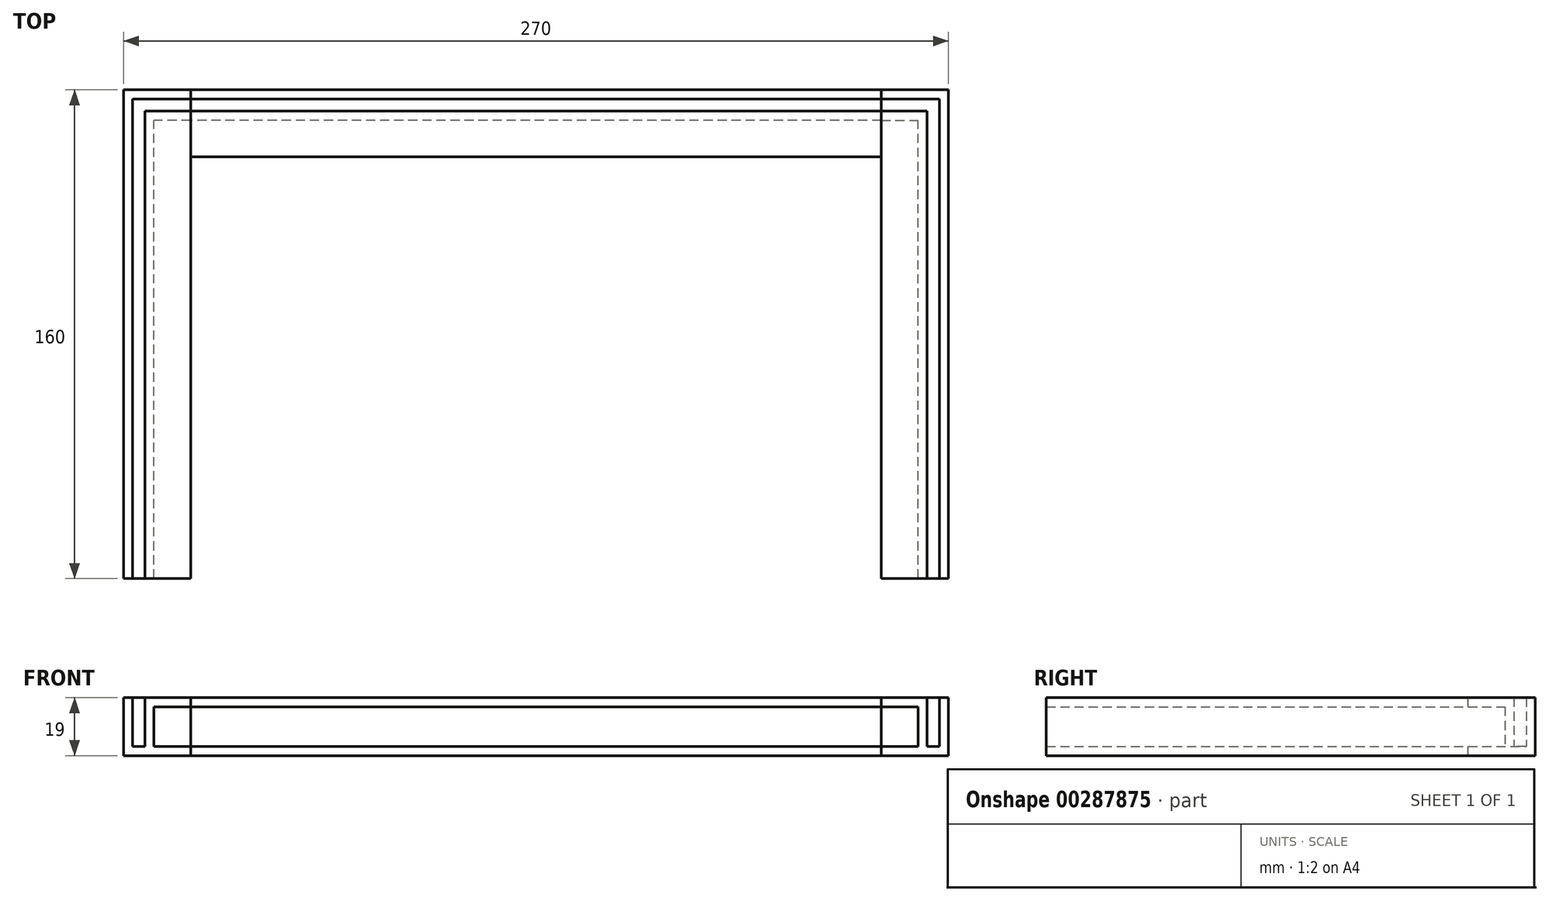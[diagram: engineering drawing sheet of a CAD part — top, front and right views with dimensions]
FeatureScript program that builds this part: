
annotation { "Feature Type Name" : "Feature", "Feature Type Description" : "" }
export const myFeature = defineFeature(function(context is Context, id is Id, definition is map)
    precondition{}
    {
        {
            var Q0;
            Q0=qCreatedBy(makeId("Front.planeOp"),FACE);
            var sketch = newSketch(context, id + "F0", { "sketchPlane" : qUnion([Q0])});
            skLineSegment(sketch, "E0", {"start": v(0, 0) * mm, "end": v(0, 19) * mm});
            skLineSegment(sketch, "E1", {"start": v(0, 19) * mm, "end": v(3, 19) * mm});
            skLineSegment(sketch, "E2", {"start": v(3, 19) * mm, "end": v(3, 3) * mm});
            skLineSegment(sketch, "E3", {"start": v(3, 3) * mm, "end": v(7, 3) * mm});
            skLineSegment(sketch, "E4", {"start": v(7, 3) * mm, "end": v(7, 19) * mm});
            skLineSegment(sketch, "E5", {"start": v(7, 19) * mm, "end": v(22, 19) * mm});
            skLineSegment(sketch, "E6", {"start": v(22, 19) * mm, "end": v(22, 16) * mm});
            skLineSegment(sketch, "E7", {"start": v(22, 16) * mm, "end": v(10, 16) * mm});
            skLineSegment(sketch, "E8", {"start": v(10, 16) * mm, "end": v(10, 3) * mm});
            skLineSegment(sketch, "E9", {"start": v(10, 3) * mm, "end": v(22, 3) * mm});
            skLineSegment(sketch, "E10", {"start": v(22, 3) * mm, "end": v(22, 0) * mm});
            skLineSegment(sketch, "E11", {"start": v(22, 0) * mm, "end": v(0, 0) * mm});
            skSolve(sketch);
        }
        {
            var Q0;
            Q0 = qSketchRegion(id + "F0", true);
            extrude(context, id + "F1", {"entities" : qUnion([Q0]), "depth" : 160 * mm});
        }
        {
            var Q0;
            Q0=makeQuery(id+"F1.opExtrude","SWEPT_FACE",FACE,{"disambiguationData":[OSD([sQuery(id+"F0.wireOp",EDGE,"E8")])]});
            var sketch = newSketch(context, id + "F2", { "sketchPlane" : qUnion([Q0])});
            skLineSegment(sketch, "E12.bottom", {"start": v(0, 16) * mm, "end": v(-10, 16) * mm});
            skLineSegment(sketch, "E12.top", {"start": v(0, 3) * mm, "end": v(-10, 3) * mm});
            skLineSegment(sketch, "E12.left", {"start": v(0, 16) * mm, "end": v(0, 3) * mm});
            skLineSegment(sketch, "E12.right", {"start": v(-10, 16) * mm, "end": v(-10, 3) * mm});
            skSolve(sketch);
        }
        {
            var Q0;
            Q0 = qSketchRegion(id + "F2", true);
            var Q1;
            Q1=makeQuery(id+"F1.opExtrude","SWEPT_FACE",FACE,{"disambiguationData":[OSD([sQuery(id+"F0.wireOp",EDGE,"E6")])]});
            extrude(context, id + "F3", {"entities" : qUnion([Q0]), "operationType" : NewBodyOperationType.ADD, "endBound" : BoundingType.UP_TO_SURFACE, "endBoundEntityFace" : qUnion([Q1]), "depth" : 25 * mm});
        }
        {
            var Q0;
            Q0=makeQuery(id+"F3.boolean.opBoolean","MERGE",FACE,{"derivedFrom":[makeQuery(id+"F1.opExtrude","CAP_FACE",FACE,{"disambiguationData":[OSD([sQuery(id+"F0.wireOp",EDGE,"E0"),sQuery(id+"F0.wireOp",EDGE,"E1"),sQuery(id+"F0.wireOp",EDGE,"E2"),sQuery(id+"F0.wireOp",EDGE,"E3"),sQuery(id+"F0.wireOp",EDGE,"E4"),sQuery(id+"F0.wireOp",EDGE,"E5"),sQuery(id+"F0.wireOp",EDGE,"E6"),sQuery(id+"F0.wireOp",EDGE,"E7"),sQuery(id+"F0.wireOp",EDGE,"E8"),sQuery(id+"F0.wireOp",EDGE,"E9"),sQuery(id+"F0.wireOp",EDGE,"E10"),sQuery(id+"F0.wireOp",EDGE,"E11")])],"isStart":true}),makeQuery(id+"F3.opExtrude","SWEPT_FACE",FACE,{"disambiguationData":[OSD([sQuery(id+"F2.wireOp",EDGE,"E12.left")])]})]});
            var sketch = newSketch(context, id + "F4", { "sketchPlane" : qUnion([Q0])});
            skLineSegment(sketch, "E13.bottom", {"start": v(-7, 19) * mm, "end": v(-3, 19) * mm});
            skLineSegment(sketch, "E13.top", {"start": v(-7, 3) * mm, "end": v(-3, 3) * mm});
            skLineSegment(sketch, "E13.left", {"start": v(-7, 19) * mm, "end": v(-7, 3) * mm});
            skLineSegment(sketch, "E13.right", {"start": v(-3, 19) * mm, "end": v(-3, 3) * mm});
            skSolve(sketch);
        }
        {
            var Q0;
            Q0 = qSketchRegion(id + "F4", true);
            extrude(context, id + "F5", {"entities" : qUnion([Q0]), "operationType" : NewBodyOperationType.ADD, "oppositeDirection" : true, "depth" : 3 * mm});
        }
        {
            var Q0;
            Q0=makeQuery(id+"F3.boolean.opBoolean","MERGE",FACE,{"derivedFrom":[makeQuery(id+"F1.opExtrude","SWEPT_FACE",FACE,{"disambiguationData":[OSD([sQuery(id+"F0.wireOp",EDGE,"E6")])]}),makeQuery(id+"F1.opExtrude","SWEPT_FACE",FACE,{"disambiguationData":[OSD([sQuery(id+"F0.wireOp",EDGE,"E10")])]}),makeQuery(id+"F3.opExtrude","CAP_FACE",FACE,{"disambiguationData":[OSD([sQuery(id+"F2.wireOp",EDGE,"E12.bottom"),sQuery(id+"F2.wireOp",EDGE,"E12.top"),sQuery(id+"F2.wireOp",EDGE,"E12.left"),sQuery(id+"F2.wireOp",EDGE,"E12.right")])],"isStart":false})]});
            var sketch = newSketch(context, id + "F6", { "sketchPlane" : qUnion([Q0])});
            skLineSegment(sketch, "E14.bottom", {"start": v(-3, 19) * mm, "end": v(-7, 19) * mm});
            skLineSegment(sketch, "E14.top", {"start": v(-3, 3) * mm, "end": v(-7, 3) * mm});
            skLineSegment(sketch, "E14.left", {"start": v(-3, 19) * mm, "end": v(-3, 3) * mm});
            skLineSegment(sketch, "E14.right", {"start": v(-7, 19) * mm, "end": v(-7, 3) * mm});
            skSolve(sketch);
        }
        {
            var Q0;
            Q0 = qSketchRegion(id + "F6", true);
            var Q1;
            Q1=makeQuery(id+"F1.opExtrude","SWEPT_FACE",FACE,{"disambiguationData":[OSD([sQuery(id+"F0.wireOp",EDGE,"E2")])]});
            extrude(context, id + "F7", {"entities" : qUnion([Q0]), "operationType" : NewBodyOperationType.REMOVE, "endBound" : BoundingType.UP_TO_SURFACE, "oppositeDirection" : true, "endBoundEntityFace" : qUnion([Q1]), "depth" : 25 * mm});
        }
        {
            var Q0;
            Q0=makeQuery(id+"F3.boolean.opBoolean","MERGE",FACE,{"derivedFrom":[makeQuery(id+"F1.opExtrude","SWEPT_FACE",FACE,{"disambiguationData":[OSD([sQuery(id+"F0.wireOp",EDGE,"E6")])]}),makeQuery(id+"F1.opExtrude","SWEPT_FACE",FACE,{"disambiguationData":[OSD([sQuery(id+"F0.wireOp",EDGE,"E10")])]}),makeQuery(id+"F3.opExtrude","CAP_FACE",FACE,{"disambiguationData":[OSD([sQuery(id+"F2.wireOp",EDGE,"E12.bottom"),sQuery(id+"F2.wireOp",EDGE,"E12.top"),sQuery(id+"F2.wireOp",EDGE,"E12.left"),sQuery(id+"F2.wireOp",EDGE,"E12.right")])],"isStart":false})]});
            var sketch = newSketch(context, id + "F8", { "sketchPlane" : qUnion([Q0])});
            skLineSegment(sketch, "E15", {"start": v(0, 19) * mm, "end": v(0, 0) * mm});
            skLineSegment(sketch, "E16", {"start": v(0, 0) * mm, "end": v(-22, 0) * mm});
            skLineSegment(sketch, "E17", {"start": v(-22, 0) * mm, "end": v(-22, 3) * mm});
            skLineSegment(sketch, "E18", {"start": v(-22, 3) * mm, "end": v(-10, 3) * mm});
            skLineSegment(sketch, "E19", {"start": v(-10, 3) * mm, "end": v(-10, 16) * mm});
            skLineSegment(sketch, "E20", {"start": v(-10, 16) * mm, "end": v(-22, 16) * mm});
            skLineSegment(sketch, "E21", {"start": v(-22, 16) * mm, "end": v(-22, 19) * mm});
            skLineSegment(sketch, "E22", {"start": v(-22, 19) * mm, "end": v(-7, 19) * mm});
            skLineSegment(sketch, "E23", {"start": v(-7, 19) * mm, "end": v(-7, 3) * mm});
            skLineSegment(sketch, "E24", {"start": v(-7, 3) * mm, "end": v(-3, 3) * mm});
            skLineSegment(sketch, "E25", {"start": v(-3, 3) * mm, "end": v(-3, 19) * mm});
            skLineSegment(sketch, "E26", {"start": v(-3, 19) * mm, "end": v(0, 19) * mm});
            skSolve(sketch);
        }
        {
            var Q0;
            Q0 = qSketchRegion(id + "F8", true);
            extrude(context, id + "F9", {"entities" : qUnion([Q0]), "depth" : 226 * mm});
        }
        {
            var Q0;
            Q0=makeQuery(id+"F9.opExtrude","SWEPT_EDGE",EDGE,{"disambiguationData":[OSD([sQuery(id+"F0.wireOp",EDGE,"E5"),sQuery(id+"F0.wireOp",EDGE,"E6"),sQuery(id+"F8.wireOp",EDGE,"E21"),sQuery(id+"F8.wireOp",EDGE,"E22")])]});
            cPoint(context, id + "F10", {"entities" : qUnion([Q0]), "parameter" : 0.5});
        }
        {
            var Q0;
            Q0=qCreatedBy(makeId("Right.planeOp"),FACE);
            var Q1;
            Q1 = qCreatedBy(id + "F10" ,VERTEX);
            cPlane(context, id + "F11", {"entities" : qUnion([Q0, Q1]), "cplaneType" : CPlaneType.PLANE_POINT, "offset" : 25 * mm, "width" : 150 * mm, "height" : 150 * mm});
        }
        {
            var Q0;
            Q0=makeQuery(id+"F1.opExtrude","SWEPT_BODY",BODY,{"disambiguationData":[OSD([sQuery(id+"F0.wireOp",EDGE,"E0"),sQuery(id+"F0.wireOp",EDGE,"E1"),sQuery(id+"F0.wireOp",EDGE,"E2"),sQuery(id+"F0.wireOp",EDGE,"E3"),sQuery(id+"F0.wireOp",EDGE,"E4"),sQuery(id+"F0.wireOp",EDGE,"E5"),sQuery(id+"F0.wireOp",EDGE,"E6"),sQuery(id+"F0.wireOp",EDGE,"E7"),sQuery(id+"F0.wireOp",EDGE,"E8"),sQuery(id+"F0.wireOp",EDGE,"E9"),sQuery(id+"F0.wireOp",EDGE,"E10"),sQuery(id+"F0.wireOp",EDGE,"E11")])]});
            var Q1;
            Q1=qCreatedBy(id+"F11.planeOp",FACE);
            mirror(context, id + "F12", {"entities" : qUnion([Q0]), "mirrorPlane" : qUnion([Q1])});
        }
    });
